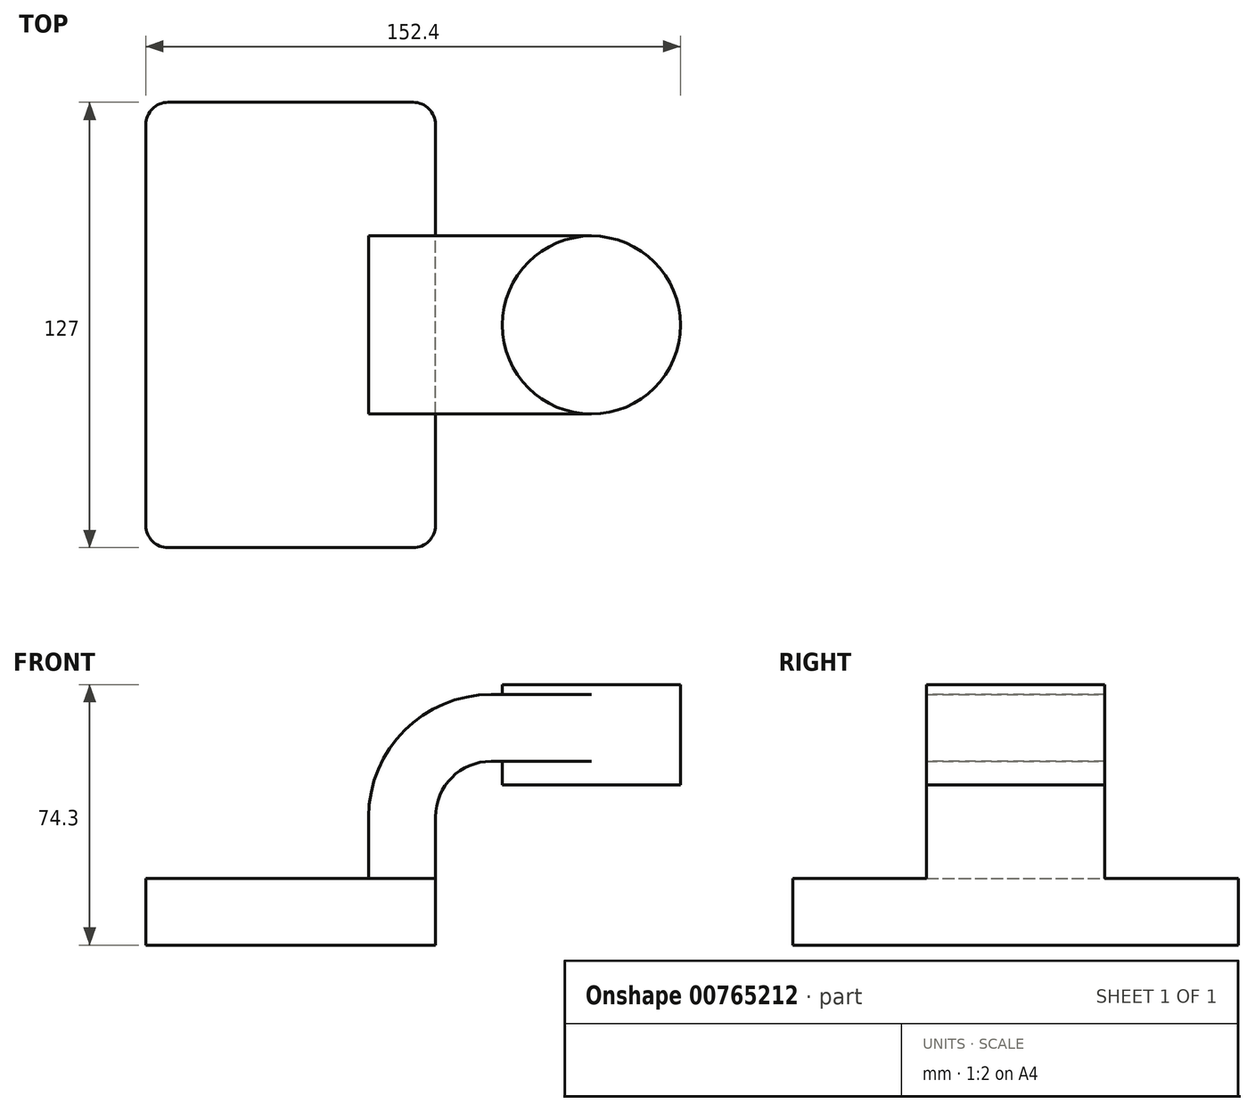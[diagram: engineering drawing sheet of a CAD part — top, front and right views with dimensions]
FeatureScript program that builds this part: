
annotation { "Feature Type Name" : "Feature", "Feature Type Description" : "" }
export const myFeature = defineFeature(function(context is Context, id is Id, definition is map)
    precondition{}
    {
        {
            var Q0;
            Q0=qCreatedBy(makeId("Front.planeOp"),FACE);
            var sketch = newSketch(context, id + "F0", { "sketchPlane" : qUnion([Q0])});
            skLineSegment(sketch, "E0.bottom", {"start": v(41.28, -9.52) * mm, "end": v(-41.28, -9.53) * mm});
            skLineSegment(sketch, "E0.top", {"start": v(41.28, 9.53) * mm, "end": v(-41.28, 9.53) * mm});
            skLineSegment(sketch, "E0.left", {"start": v(41.28, -9.52) * mm, "end": v(41.28, 9.53) * mm});
            skLineSegment(sketch, "E0.right", {"start": v(-41.28, -9.53) * mm, "end": v(-41.28, 9.53) * mm});
            skPoint(sketch, "E0.middle", {"position": v(0, 0) * mm});
            skLineSegment(sketch, "E1.bottom", {"start": v(60.32, 36.2) * mm, "end": v(111.12, 36.2) * mm});
            skLineSegment(sketch, "E1.top", {"start": v(60.32, 64.77) * mm, "end": v(111.12, 64.77) * mm});
            skLineSegment(sketch, "E1.left", {"start": v(60.32, 36.2) * mm, "end": v(60.32, 64.77) * mm});
            skLineSegment(sketch, "E1.right", {"start": v(111.12, 36.2) * mm, "end": v(111.12, 64.77) * mm});
            skPoint(sketch, "E1.middle", {"position": v(85.72, 50.48) * mm});
            skLineSegment(sketch, "E2", {"start": v(41.28, 9.53) * mm, "end": v(41.28, 27) * mm});
            skArc(sketch, "E3", {"start": v(41.27, 27) * mm, "mid": v(45.92, 38.23) * mm, "end": v(57.15, 42.88) * mm});
            skLineSegment(sketch, "E4", {"start": v(57.15, 42.88) * mm, "end": v(85.73, 42.88) * mm});
            skLineSegment(sketch, "E5.0", {"start": v(57.15, 61.93) * mm, "end": v(85.72, 61.93) * mm});
            skArc(sketch, "E5.1", {"start": v(22.23, 27) * mm, "mid": v(32.45, 51.7) * mm, "end": v(57.15, 61.93) * mm});
            skLineSegment(sketch, "E5.2", {"start": v(22.23, 9.53) * mm, "end": v(22.23, 27) * mm});
            skLineSegment(sketch, "E6", {"start": v(85.72, 50.48) * mm, "end": v(85.72, 64.77) * mm});
            skLineSegment(sketch, "E7", {"start": v(85.72, 64.77) * mm, "end": v(85.72, 36.2) * mm});
            skLineSegment(sketch, "E8", {"start": v(85.73, 42.88) * mm, "end": v(85.72, 42.88) * mm});
            skFitSpline(sketch, "E9", {"points": [v(-41.28, 9.53) * mm, v(57.15, 61.93) * mm], "startDerivative": vector(0.08, 86.33) * mm, "endDerivative": vector(112.61, -14.98) * mm});
            skSolve(sketch);
        }
        {
            var Q0;
            Q0=makeQuery(id+"F0.imprint","IMPRINT",FACE,{"disambiguationData":[TD([[makeQuery(id+"F0.imprint","IMPRINT",EDGE,{"derivedFrom":sQuery(id+"F0.wireOp",EDGE,"E0.bottom")}),-1.0]])]});
            extrude(context, id + "F1", {"entities" : qUnion([Q0]), "endBound" : BoundingType.SYMMETRIC, "depth" : 127 * mm, "offsetDistance" : 25.4 * mm});
        }
        {
            var Q0;
            {var subQ0=sQuery(id+"F0.wireOp",EDGE,"E2");Q0=makeQuery(id+"F0.imprint","IMPRINT",FACE,{"disambiguationData":[TD([[makeQuery(id+"F0.imprint","IMPRINT",EDGE,{"derivedFrom":subQ0}),1.0]])]});}
            var Q1;
            {var subQ5=sQuery(id+"F0.wireOp",EDGE,"E1.left");var subQ7=sQuery(id+"F0.wireOp",EDGE,"E4");var subQ8=makeQuery(id+"F0.imprint","INTERSECT",VERTEX,{"derivedFrom":[subQ5,subQ7]});Q1=makeQuery(id+"F0.imprint","IMPRINT",FACE,{"disambiguationData":[TD([[makeQuery(id+"F0.imprint","IMPRINT",EDGE,{"disambiguationData":[TD([[subQ8,-1.0]])],"derivedFrom":subQ5}),-1.0]])]});}
            extrude(context, id + "F2", {"entities" : qUnion([Q0, Q1]), "operationType" : NewBodyOperationType.ADD, "endBound" : BoundingType.SYMMETRIC, "depth" : 50.8 * mm, "offsetDistance" : 25.4 * mm});
        }
        {
            var Q0;
            Q0=makeQuery(id+"F0.imprint","IMPRINT",FACE,{"disambiguationData":[TD([[makeQuery(id+"F0.imprint","IMPRINT",EDGE,{"derivedFrom":sQuery(id+"F0.wireOp",EDGE,"E5.1")}),1.0]])]});
            extrude(context, id + "F3", {"entities" : qUnion([Q0]), "operationType" : NewBodyOperationType.ADD, "endBound" : BoundingType.SYMMETRIC, "depth" : 15.88 * mm, "offsetDistance" : 25.4 * mm});
        }
        {
            var Q0;
            {var subQ0=sQuery(id+"F0.wireOp",EDGE,"E1.right");Q0=makeQuery(id+"F0.imprint","IMPRINT",FACE,{"disambiguationData":[TD([[makeQuery(id+"F0.imprint","IMPRINT",EDGE,{"derivedFrom":subQ0}),1.0]])]});}
            var Q1;
            Q1=sQuery(id+"F0.wireOp",EDGE,"E7");
            revolve(context, id + "F4", {"operationType" : NewBodyOperationType.ADD, "surfaceOperationType" : NewSurfaceOperationType.NEW, "entities" : qUnion([Q0]), "axis" : qUnion([Q1]), "revolveType" : RevolveType.FULL});
        }
        {
            var Q0;
            Q0=makeQuery(id+"F1.opExtrude","CAP_EDGE",EDGE,{"disambiguationData":[OSD([sQuery(id+"F0.wireOp",EDGE,"E0.right")])],"isStart":false});
            var Q1;
            Q1=makeQuery(id+"F1.opExtrude","CAP_EDGE",EDGE,{"disambiguationData":[OSD([sQuery(id+"F0.wireOp",EDGE,"E0.left")])],"isStart":false});
            var Q2;
            Q2=makeQuery(id+"F1.opExtrude","CAP_EDGE",EDGE,{"disambiguationData":[OSD([sQuery(id+"F0.wireOp",EDGE,"E0.left")])],"isStart":true});
            var Q3;
            Q3=makeQuery(id+"F1.opExtrude","CAP_EDGE",EDGE,{"disambiguationData":[OSD([sQuery(id+"F0.wireOp",EDGE,"E0.right")])],"isStart":true});
            fillet(context, id + "F5", {"entities" : qUnion([Q0, Q1, Q2, Q3]), "radius" : 6.35 * mm, "tangentPropagation" : true, "allowEdgeOverflow" : false});
        }
    });
